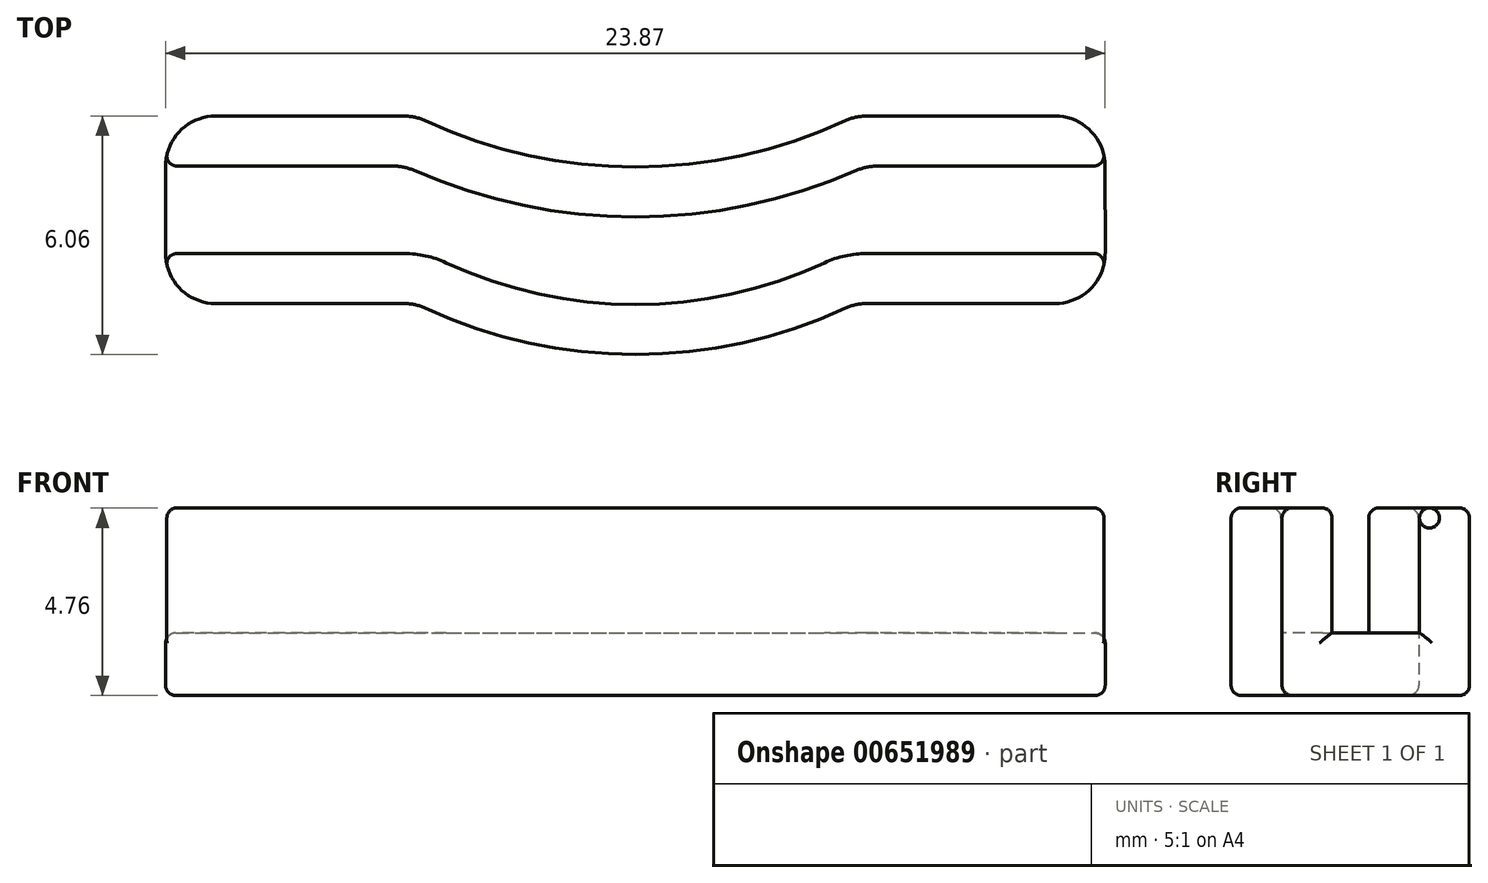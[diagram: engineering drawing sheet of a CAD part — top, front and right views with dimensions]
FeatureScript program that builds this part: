
annotation { "Feature Type Name" : "Feature", "Feature Type Description" : "" }
export const myFeature = defineFeature(function(context is Context, id is Id, definition is map)
    precondition{}
    {
        {
            var Q0;
            Q0=qCreatedBy(makeId("Top.planeOp"),FACE);
            var sketch = newSketch(context, id + "F0", { "sketchPlane" : qUnion([Q0])});
            skLineSegment(sketch, "E0", {"start": v(-9.9, 0) * mm, "end": v(-5.1, 0) * mm});
            skLineSegment(sketch, "E1", {"start": v(11.43, 0) * mm, "end": v(6.64, 0) * mm});
            skArc(sketch, "E2", {"start": v(-4.57, -0.12) * mm, "mid": v(0.77, -1.3) * mm, "end": v(6.1, -0.12) * mm});
            skPoint(sketch, "E2.third.point", {"position": v(0, -1.27) * mm});
            skLineSegment(sketch, "E3", {"start": v(-9.9, -4.76) * mm, "end": v(-5.1, -4.76) * mm});
            skLineSegment(sketch, "E4", {"start": v(11.43, -4.76) * mm, "end": v(6.64, -4.76) * mm});
            skArc(sketch, "E5", {"start": v(-4.57, -4.88) * mm, "mid": v(0.77, -6.06) * mm, "end": v(6.1, -4.88) * mm});
            skPoint(sketch, "E5.third.point", {"position": v(0.77, -6.06) * mm});
            skLineSegment(sketch, "E6", {"start": v(-11.17, -1.27) * mm, "end": v(-11.17, -3.5) * mm});
            skLineSegment(sketch, "E7", {"start": v(12.7, -3.5) * mm, "end": v(12.7, -1.27) * mm});
            skPoint(sketch, "E8.visualSharp", {"position": v(-11.17, 0) * mm});
            skArc(sketch, "E8.filletArc", {"start": v(-9.9, 0) * mm, "mid": v(-10.8, -0.37) * mm, "end": v(-11.17, -1.27) * mm});
            skPoint(sketch, "E9.visualSharp", {"position": v(-11.17, -4.76) * mm});
            skArc(sketch, "E9.filletArc", {"start": v(-11.17, -3.5) * mm, "mid": v(-10.8, -4.4) * mm, "end": v(-9.9, -4.76) * mm});
            skPoint(sketch, "E10.visualSharp", {"position": v(12.7, -4.76) * mm});
            skArc(sketch, "E10.filletArc", {"start": v(11.43, -4.76) * mm, "mid": v(12.33, -4.4) * mm, "end": v(12.7, -3.5) * mm});
            skPoint(sketch, "E11.visualSharp", {"position": v(12.7, 0) * mm});
            skArc(sketch, "E11.filletArc", {"start": v(12.7, -1.27) * mm, "mid": v(12.33, -0.37) * mm, "end": v(11.43, 0) * mm});
            skPoint(sketch, "E12.visualSharp", {"position": v(-4.82, 0) * mm});
            skArc(sketch, "E12.filletArc", {"start": v(-4.57, -0.12) * mm, "mid": v(-4.83, -0.03) * mm, "end": v(-5.1, 0) * mm});
            skPoint(sketch, "E13.visualSharp", {"position": v(6.35, 0) * mm});
            skArc(sketch, "E13.filletArc", {"start": v(6.64, 0) * mm, "mid": v(6.36, -0.03) * mm, "end": v(6.1, -0.12) * mm});
            skPoint(sketch, "E14.visualSharp", {"position": v(6.36, -4.76) * mm});
            skArc(sketch, "E14.filletArc", {"start": v(6.64, -4.76) * mm, "mid": v(6.37, -4.8) * mm, "end": v(6.1, -4.88) * mm});
            skPoint(sketch, "E15.visualSharp", {"position": v(-4.82, -4.76) * mm});
            skArc(sketch, "E15.filletArc", {"start": v(-4.57, -4.88) * mm, "mid": v(-4.83, -4.8) * mm, "end": v(-5.1, -4.76) * mm});
            skSolve(sketch);
        }
        {
            var Q0;
            Q0=qSketchRegion(id+"F0",true);
            extrude(context, id + "F1", {"entities" : qUnion([Q0]), "depth" : 1.59 * mm, "offsetDistance" : 25.4 * mm});
        }
        {
            var Q0;
            Q0=makeQuery(id+"F1.opExtrude","CAP_FACE",FACE,{"disambiguationData":[OSD([sQuery(id+"F0.wireOp",EDGE,"E0"),sQuery(id+"F0.wireOp",EDGE,"E1"),sQuery(id+"F0.wireOp",EDGE,"E2"),sQuery(id+"F0.wireOp",EDGE,"E3"),sQuery(id+"F0.wireOp",EDGE,"E4"),sQuery(id+"F0.wireOp",EDGE,"E5"),sQuery(id+"F0.wireOp",EDGE,"E6"),sQuery(id+"F0.wireOp",EDGE,"E7"),sQuery(id+"F0.wireOp",EDGE,"E8.filletArc"),sQuery(id+"F0.wireOp",EDGE,"E9.filletArc"),sQuery(id+"F0.wireOp",EDGE,"E10.filletArc"),sQuery(id+"F0.wireOp",EDGE,"E11.filletArc"),sQuery(id+"F0.wireOp",EDGE,"E12.filletArc"),sQuery(id+"F0.wireOp",EDGE,"E13.filletArc"),sQuery(id+"F0.wireOp",EDGE,"E14.filletArc"),sQuery(id+"F0.wireOp",EDGE,"E15.filletArc")])],"isStart":false});
            var sketch = newSketch(context, id + "F2", { "sketchPlane" : qUnion([Q0])});
            skArc(sketch, "E16.0", {"start": v(5.57, -3.73) * mm, "mid": v(6.1, -3.55) * mm, "end": v(6.64, -3.5) * mm});
            skArc(sketch, "E16.1", {"start": v(-4.04, -3.73) * mm, "mid": v(0.77, -4.79) * mm, "end": v(5.57, -3.73) * mm});
            skArc(sketch, "E16.2", {"start": v(-5.1, -3.5) * mm, "mid": v(-4.56, -3.55) * mm, "end": v(-4.04, -3.73) * mm});
            skLineSegment(sketch, "E16.3", {"start": v(-9.9, -3.5) * mm, "end": v(-5.1, -3.5) * mm});
            skLineSegment(sketch, "E16.4", {"start": v(-9.9, -3.5) * mm, "end": v(-9.9, -3.5) * mm});
            skLineSegment(sketch, "E16.5", {"start": v(11.43, -1.27) * mm, "end": v(6.91, -1.27) * mm});
            skLineSegment(sketch, "E16.6", {"start": v(11.43, -1.27) * mm, "end": v(11.43, -1.27) * mm});
            skLineSegment(sketch, "E16.8", {"start": v(11.43, -3.5) * mm, "end": v(11.43, -3.5) * mm});
            skArc(sketch, "E16.10", {"start": v(6.4, -1.38) * mm, "mid": v(0.77, -2.56) * mm, "end": v(-4.86, -1.38) * mm});
            skLineSegment(sketch, "E16.12", {"start": v(-5.38, -1.27) * mm, "end": v(-9.9, -1.27) * mm});
            skLineSegment(sketch, "E16.13", {"start": v(-9.9, -1.27) * mm, "end": v(-9.9, -1.27) * mm});
            skLineSegment(sketch, "E16.14", {"start": v(6.64, -3.5) * mm, "end": v(11.43, -3.5) * mm});
            skLineSegment(sketch, "E17.0", {"start": v(-9.9, 0) * mm, "end": v(-5.1, 0) * mm});
            skArc(sketch, "E17.1", {"start": v(-4.57, -0.12) * mm, "mid": v(-4.83, -0.03) * mm, "end": v(-5.1, 0) * mm});
            skArc(sketch, "E17.2", {"start": v(-4.57, -0.12) * mm, "mid": v(0.77, -1.3) * mm, "end": v(6.1, -0.12) * mm});
            skArc(sketch, "E17.3", {"start": v(-4.57, -4.88) * mm, "mid": v(0.77, -6.06) * mm, "end": v(6.1, -4.88) * mm});
            skArc(sketch, "E17.4", {"start": v(-4.57, -4.88) * mm, "mid": v(-4.83, -4.8) * mm, "end": v(-5.1, -4.76) * mm});
            skLineSegment(sketch, "E17.5", {"start": v(-9.9, -4.76) * mm, "end": v(-5.1, -4.76) * mm});
            skArc(sketch, "E17.6", {"start": v(-11.17, -3.5) * mm, "mid": v(-10.8, -4.4) * mm, "end": v(-9.9, -4.76) * mm});
            skArc(sketch, "E17.8", {"start": v(-9.9, 0) * mm, "mid": v(-10.8, -0.37) * mm, "end": v(-11.17, -1.27) * mm});
            skArc(sketch, "E17.9", {"start": v(6.64, -4.76) * mm, "mid": v(6.37, -4.8) * mm, "end": v(6.1, -4.88) * mm});
            skLineSegment(sketch, "E17.10", {"start": v(11.43, -4.76) * mm, "end": v(6.64, -4.76) * mm});
            skArc(sketch, "E17.12", {"start": v(11.43, -4.76) * mm, "mid": v(12.33, -4.4) * mm, "end": v(12.7, -3.5) * mm});
            skArc(sketch, "E17.13", {"start": v(12.7, -1.27) * mm, "mid": v(12.33, -0.37) * mm, "end": v(11.43, 0) * mm});
            skLineSegment(sketch, "E17.14", {"start": v(11.43, 0) * mm, "end": v(6.64, 0) * mm});
            skArc(sketch, "E17.15", {"start": v(6.64, 0) * mm, "mid": v(6.36, -0.03) * mm, "end": v(6.1, -0.12) * mm});
            skLineSegment(sketch, "E18", {"start": v(-9.9, -1.27) * mm, "end": v(-11.17, -1.27) * mm});
            skLineSegment(sketch, "E19", {"start": v(-9.9, -3.5) * mm, "end": v(-11.17, -3.5) * mm});
            skLineSegment(sketch, "E20", {"start": v(11.43, -3.5) * mm, "end": v(12.7, -3.5) * mm});
            skLineSegment(sketch, "E21", {"start": v(11.43, -1.27) * mm, "end": v(12.7, -1.27) * mm});
            skArc(sketch, "E22.filletArc", {"start": v(-4.86, -1.38) * mm, "mid": v(-5.12, -1.3) * mm, "end": v(-5.38, -1.27) * mm});
            skArc(sketch, "E23.filletArc", {"start": v(6.91, -1.27) * mm, "mid": v(6.65, -1.3) * mm, "end": v(6.4, -1.38) * mm});
            skSolve(sketch);
        }
        {
            var Q0;
            Q0=qSketchRegion(id+"F2",true);
            extrude(context, id + "F3", {"entities" : qUnion([Q0]), "operationType" : NewBodyOperationType.ADD, "depth" : 3.17 * mm, "offsetDistance" : 25.4 * mm});
        }
        {
            var Q0;
            Q0=makeQuery(id+"F1.opExtrude","CAP_EDGE",EDGE,{"disambiguationData":[OSD([sQuery(id+"F0.wireOp",EDGE,"E7")])],"isStart":false});
            var Q1;
            Q1=makeQuery(id+"F3.opExtrude","SWEPT_EDGE",EDGE,{"disambiguationData":[OSD([sQuery(id+"F0.wireOp",EDGE,"E7"),sQuery(id+"F2.wireOp",EDGE,"E17.13"),sQuery(id+"F2.wireOp",EDGE,"E21")])]});
            var Q2;
            Q2=makeQuery(id+"F3.opExtrude","SWEPT_EDGE",EDGE,{"disambiguationData":[OSD([sQuery(id+"F0.wireOp",EDGE,"E7"),sQuery(id+"F2.wireOp",EDGE,"E17.12"),sQuery(id+"F2.wireOp",EDGE,"E20")])]});
            var Q3;
            Q3=makeQuery(id+"F3.opExtrude","SWEPT_EDGE",EDGE,{"disambiguationData":[OSD([sQuery(id+"F2.wireOp",EDGE,"E16.5"),sQuery(id+"F2.wireOp",EDGE,"E16.10")])]});
            var Q4;
            Q4=makeQuery(id+"F1.opExtrude","CAP_EDGE",EDGE,{"disambiguationData":[OSD([sQuery(id+"F0.wireOp",EDGE,"E7")])],"isStart":true});
            var Q5;
            Q5=makeQuery(id+"F3.opExtrude","SWEPT_EDGE",EDGE,{"disambiguationData":[OSD([sQuery(id+"F0.wireOp",EDGE,"E6"),sQuery(id+"F2.wireOp",EDGE,"E17.8"),sQuery(id+"F2.wireOp",EDGE,"E18")])]});
            var Q6;
            Q6=makeQuery(id+"F3.opExtrude","SWEPT_EDGE",EDGE,{"disambiguationData":[OSD([sQuery(id+"F0.wireOp",EDGE,"E6"),sQuery(id+"F2.wireOp",EDGE,"E17.6"),sQuery(id+"F2.wireOp",EDGE,"E19")])]});
            var Q7;
            Q7=makeQuery(id+"F3.opExtrude","CAP_EDGE",EDGE,{"disambiguationData":[OSD([sQuery(id+"F2.wireOp",EDGE,"E16.1")])],"isStart":false});
            var Q8;
            Q8=makeQuery(id+"F3.opExtrude","CAP_EDGE",EDGE,{"disambiguationData":[OSD([sQuery(id+"F2.wireOp",EDGE,"E17.5")])],"isStart":false});
            var Q9;
            Q9=makeQuery(id+"F3.opExtrude","CAP_EDGE",EDGE,{"disambiguationData":[OSD([sQuery(id+"F2.wireOp",EDGE,"E17.0")])],"isStart":false});
            var Q10;
            Q10=makeQuery(id+"F3.opExtrude","CAP_EDGE",EDGE,{"disambiguationData":[OSD([sQuery(id+"F2.wireOp",EDGE,"E16.10")])],"isStart":false});
            var Q11;
            Q11=makeQuery(id+"F3.opExtrude","CAP_EDGE",EDGE,{"disambiguationData":[OSD([sQuery(id+"F2.wireOp",EDGE,"E16.12")])],"isStart":false});
            var Q12;
            Q12=makeQuery(id+"F3.opExtrude","CAP_EDGE",EDGE,{"disambiguationData":[OSD([sQuery(id+"F2.wireOp",EDGE,"E17.8")])],"isStart":false});
            var Q13;
            Q13=makeQuery(id+"F3.opExtrude","CAP_EDGE",EDGE,{"disambiguationData":[OSD([sQuery(id+"F2.wireOp",EDGE,"E18")])],"isStart":false});
            var Q14;
            Q14=makeQuery(id+"F1.opExtrude","CAP_EDGE",EDGE,{"disambiguationData":[OSD([sQuery(id+"F0.wireOp",EDGE,"E6")])],"isStart":false});
            fillet(context, id + "F4", {"entities" : qUnion([Q0, Q1, Q2, Q3, Q4, Q5, Q6, Q7, Q8, Q9, Q10, Q11, Q12, Q13, Q14]), "radius" : 0.25 * mm, "tangentPropagation" : true, "allowEdgeOverflow" : false});
        }
    });
